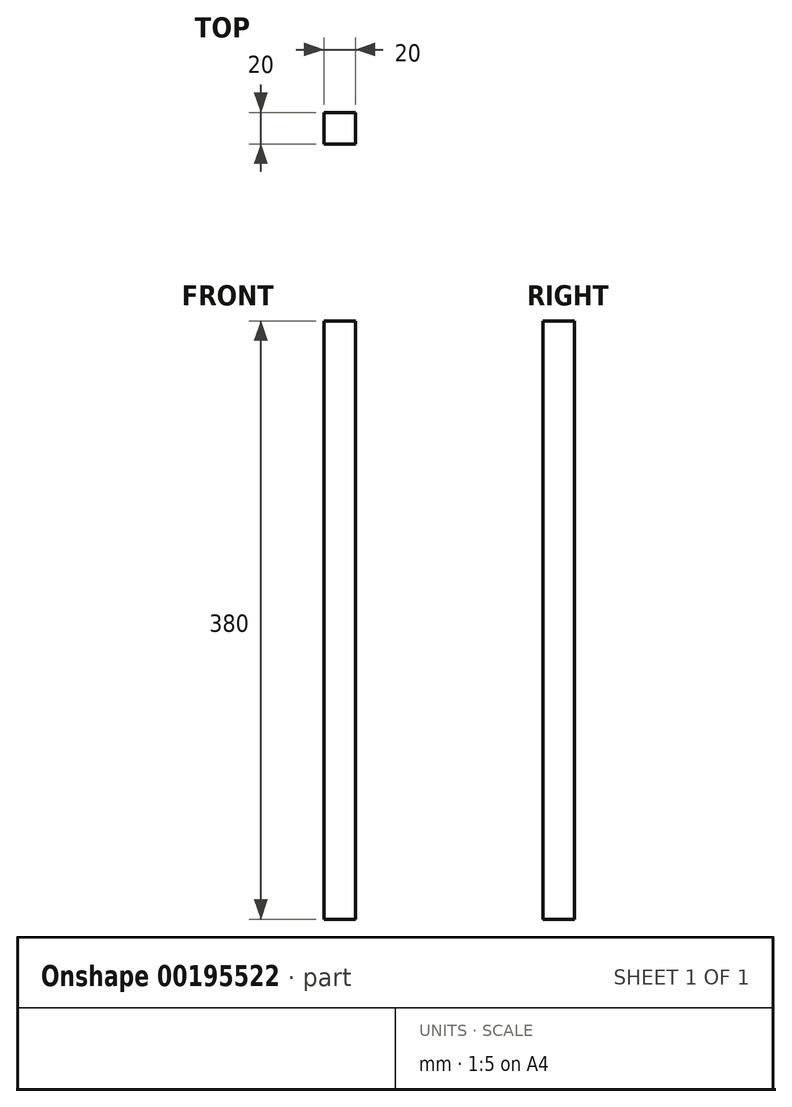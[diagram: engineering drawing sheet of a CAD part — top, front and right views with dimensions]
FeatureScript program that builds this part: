
annotation { "Feature Type Name" : "Feature", "Feature Type Description" : "" }
export const myFeature = defineFeature(function(context is Context, id is Id, definition is map)
    precondition{}
    {
        {
            var Q0;
            Q0=qCreatedBy(makeId("Top.planeOp"),FACE);
            var sketch = newSketch(context, id + "F0", { "sketchPlane" : qUnion([Q0])});
            skLineSegment(sketch, "E0.bottom", {"start": v(-99.2, -20) * mm, "end": v(-79.2, -20) * mm});
            skLineSegment(sketch, "E0.top", {"start": v(-99.2, 0) * mm, "end": v(-79.2, 0) * mm});
            skLineSegment(sketch, "E0.left", {"start": v(-99.2, -20) * mm, "end": v(-99.2, 0) * mm});
            skLineSegment(sketch, "E0.right", {"start": v(-79.2, -20) * mm, "end": v(-79.2, 0) * mm});
            skSolve(sketch);
        }
        {
            var Q0;
            Q0=makeQuery(id+"F0.imprint","IMPRINT",FACE,{"disambiguationData":[TD([[makeQuery(id+"F0.imprint","IMPRINT",EDGE,{"derivedFrom":sQuery(id+"F0.wireOp",EDGE,"E0.bottom")}),1.0]])]});
            extrude(context, id + "F1", {"entities" : qUnion([Q0]), "depth" : 380 * mm});
        }
    });
